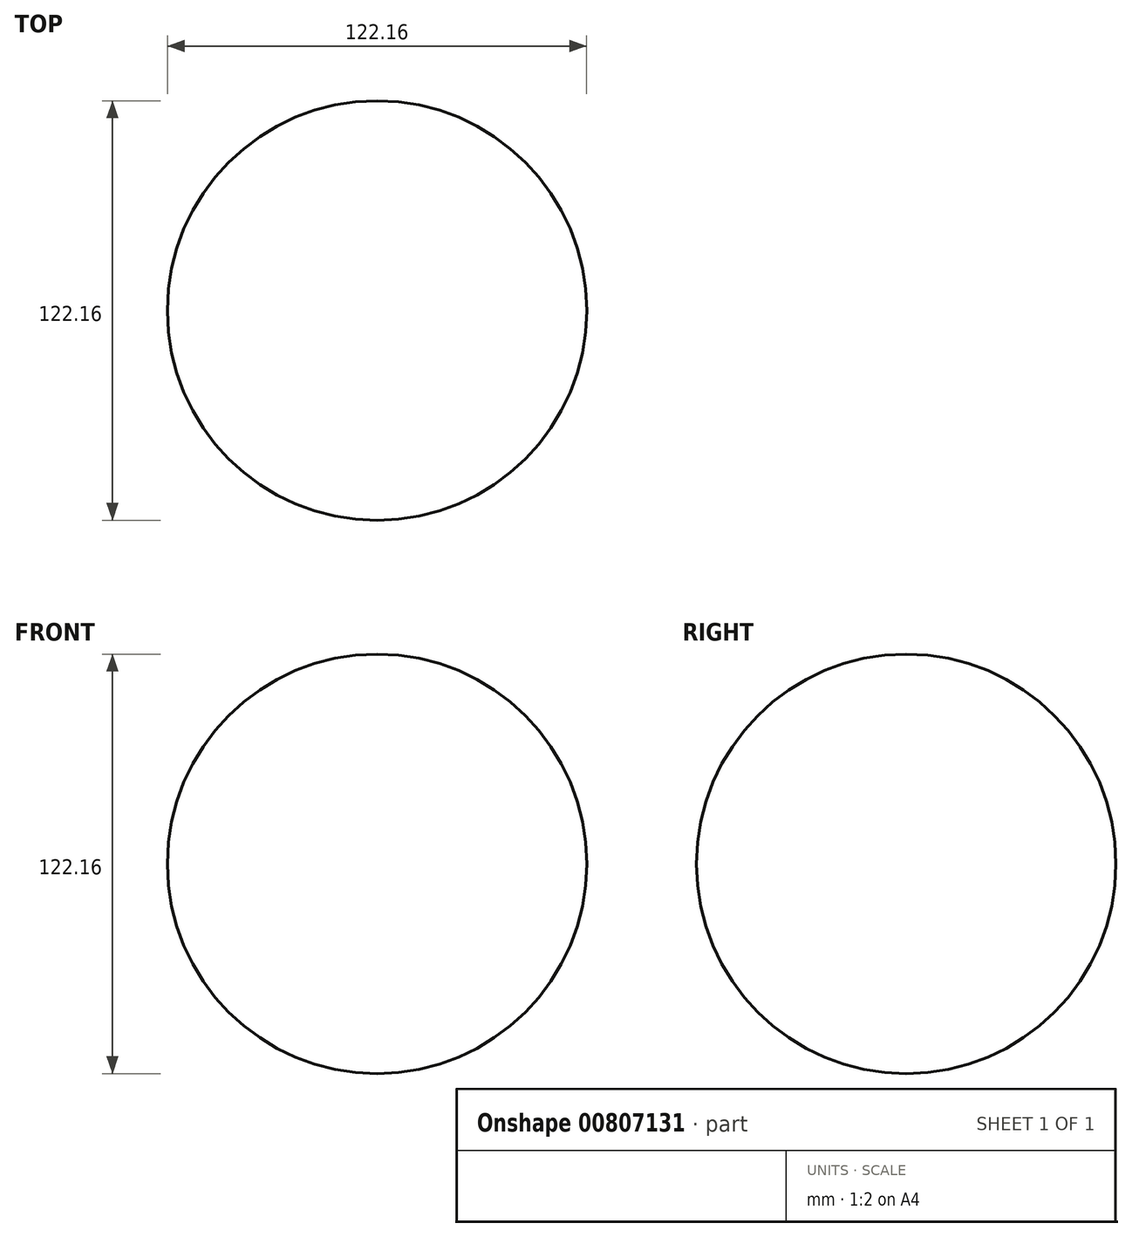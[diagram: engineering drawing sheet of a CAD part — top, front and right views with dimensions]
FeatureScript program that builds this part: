
annotation { "Feature Type Name" : "Feature", "Feature Type Description" : "" }
export const myFeature = defineFeature(function(context is Context, id is Id, definition is map)
    precondition{}
    {
        {
            var Q0;
            Q0=qCreatedBy(makeId("Front.planeOp"),FACE);
            var sketch = newSketch(context, id + "F0", { "sketchPlane" : qUnion([Q0])});
            skCircle(sketch, "E0", {"center": v(0, 0) * mm, "radius": 61.08 * mm});
            skLineSegment(sketch, "E1", {"start": v(0, 61.08) * mm, "end": v(0, -61.08) * mm});
            skSolve(sketch);
        }
        {
            var Q0;
            {var subQ0=sQuery(id+"F0.wireOp",EDGE,"E1");Q0=makeQuery(id+"F0.imprint","IMPRINT",FACE,{"disambiguationData":[TD([[makeQuery(id+"F0.imprint","IMPRINT",EDGE,{"derivedFrom":subQ0}),-1.0]])]});}
            var Q1;
            Q1=sQuery(id+"F0.wireOp",EDGE,"E1");
            revolve(context, id + "F1", {"surfaceOperationType" : NewSurfaceOperationType.NEW, "entities" : qUnion([Q0]), "axis" : qUnion([Q1]), "revolveType" : RevolveType.FULL});
        }
    });
